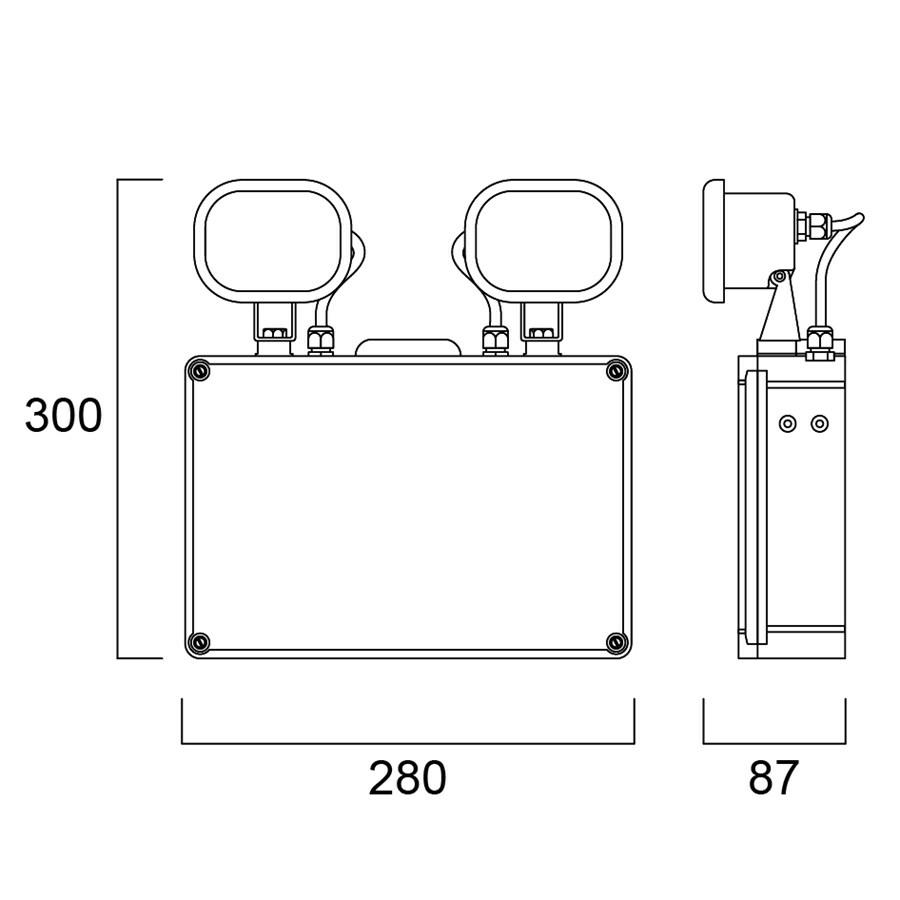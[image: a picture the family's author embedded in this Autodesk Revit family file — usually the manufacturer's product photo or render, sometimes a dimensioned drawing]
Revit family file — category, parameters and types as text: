
# Revit family: 0041770
name_source: partatom
category: Lighting Fixtures
revit_build: Autodesk Revit 2017 (Build: 20160225_1515(x64)
units: mm (PartAtom-declared; Revit-internal decimal feet)

## family parameters
Cut with Voids When Loaded = No
Host = Face
Light Source = No
OmniClass Number = 23.80.70.00
OmniClass Title = Lighting
Part Type = Normal
Room Calculation Point = No
Round Connector Dimension = Use Diameter
Shared = No

## types (1)
- 0041770 SYLSAFE TWIN TS C EM3 NM DA
    Apparent Load = 3 VA
    Assembly Code = D5020200
    AssetType = Fixed
    ClassificationName = Uniclass2015
    ClassificationValue = EF_70_80
    Cost = 0 $
    Default Elevation = 1219 mm
    Description = SylSafe Twin TS C EM3 NM DA is a dust and waterproof wall mounted twin LED projector for industrial applications. Two individually adjustable heads each delivering 200Lm. White housing colour. Non-maintained 3hr emergency operation with NiCd rechargeable battery. Recharge period 24 hours. Self testing with DALI monitoring capability.  400Lm, 3.23W, IK03, IP65, Power Factor 0.6. Class I electrical construction.
    DocumentationLiterature = http://www.sylvania-lighting.com
    ElectricShockClassification = Class I
    IfcExportAs = IfcLightFixtureType
    IfcExportType = IfcLightFixtureType
    ImpactProtectionIndex = IK03
    IngressProtection = IP65
    InputNominalFrequency = 50/60 Hz
    Keynote = 16500
    Lamp = LED
    LampColourRenderingIndex = 70
    LampColourTemperature = 5700 K
    LampNominalLuminous = 400 lm
    LampsType = LED
    LuminousEfficacy = 124 lm/W
    Manufacturer = Feilo Sylvania
    ManufacturerName = Feilo Sylvania
    Material_1_SYL = PC/ABS Plastic
    Material_2_SYL = Aluminum
    Material_3_SYL = <By Category>
    Material_4_SYL = <By Category>
    Model = SylSafe Twin TS C EM3 NM DA
    ModelNumber = 0041770
    ModelReference = SylSafe Twin TS C EM3 NM DA
    Name = SylSafe Twin TS C EM3 NM DA
    NominalDepth = 87 mm
    NominalHeight = 300 mm
    NominalLength = 280 mm  [stored 0.918635 ft]
    PowerConsumption = 3.23 W
    PowerFactor = 0.6
    Type Image = <None>
    TypeLampHead_SYL = sylsafe_twin_lamp_head : 0041770 SYLSAFE TWIN TS C EM3 NM DA
    TypeName = SylSafe Twin TS C EM3 NM DA
    URL = http://www.sylvania-lighting.com
    Voltage = 220 V
    Weight = 8.5 kg

note: [stored X ft] marks values corroborated as IEEE doubles in the binary element streams (Revit-internal decimal feet)

## geometry (parser evidence)
native form markers: Sweep x1
no freeform markers — native parametric forms only
